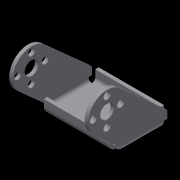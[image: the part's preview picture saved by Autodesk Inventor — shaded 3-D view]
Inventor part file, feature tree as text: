
AUTODESK INVENTOR PART (.ipt)
format: ipt  version: 2013 SP2 (Build 170200200, 200)  size: 211,456 bytes
history: native  units: in
note: dims shown in document units (in); Inventor stores cm internally (conversion verified against a paired STEP export)
features: sheet_metal_op x12, sketch x6, other x6, hole x2, plane x1, mirror x1
ambient origin geometry x8: Origin, YZ Plane, XZ Plane, XY Plane, X Axis, Y Axis, Z Axis, Center Point
bodies: Solid1 (feature_tree)
feature tree (28):
  sheet_metal_op  "Face1"
  sheet_metal_op  "Flange1"
  sheet_metal_op  "Flange2"
  sketch  "Sketch4"  dims[d7=0.1575in]
  sheet_metal_op  "Face2"
  hole  "Hole1"  [1 undecoded]
  hole  "Hole2"  [1 undecoded]
  sketch  "Sketch5"  dims[d8=0.0787in]
  plane  "Work Plane1"
  mirror  "Mirror1"
  sheet_metal_op  "Flange3"
  sketch  "Sketch1"  dims[d0=1.811in d3=1.1024in]
  other  "Plate1"
  sketch  "Sketch2"  dims[d4=0.0787in d5=0.0787in]
  other  "Plate2"
  sheet_metal_op  "Bend1"
  sheet_metal_op  "Corner1"
  sketch  "Sketch3"  dims[d6=0.0394in]
  other  "Plate3"
  sheet_metal_op  "Bend2"
  sheet_metal_op  "Corner2"
  other  "Plate4"
  sheet_metal_op  "Bend3"
  sketch  "Sketch6"  dims[d9=2.7559in d10=90.0deg d11=0.0787in d12=0.315in d13=0.0787in d14=0.0787in d15=0.0787in d16=0.0394in d17=0.1575in d18=0.0787in d19=2.7559in d20=90.0deg d21=0.0787in d22=0.315in d23=0.0787in d24=0.0787in d25=0.315in d33=1.1811in d34=135.0deg d35=0.315in d36=0.315in d37=0.315in d38=0.8661in d39=0.0787in d40=0.0787in d41=0.0394in d42=0.1575in d43=0.0787in d44=0.0787in d45=0.0in d46=0.1575in d47=0.2362in d48=0.1575in d49=0.0787in d50=90.0deg d51=0.0787in d52=0.8108in d53=0.315in d54=0.2362in d55=0.1575in d56=0.0787in d57=90.0deg d58=0.0787in d59=0.8108in d60=90.0deg d61=0.0787in d62=0.0394in d63=0.1575in d64=0.0787in d65=0.315in d66=90.0deg d67=0.0787in d68=0.315in d69=0.0787in d70=0.0787in]
  other  "Plate5"
  sheet_metal_op  "Bend4"
  sheet_metal_op  "Corner3"
  other  "Cut1"
note: 2 required parameter values undecoded (feature->parameter linkage not recoverable at this tier; creation-order binding heuristic only, values carry confidence <= 0.55)
